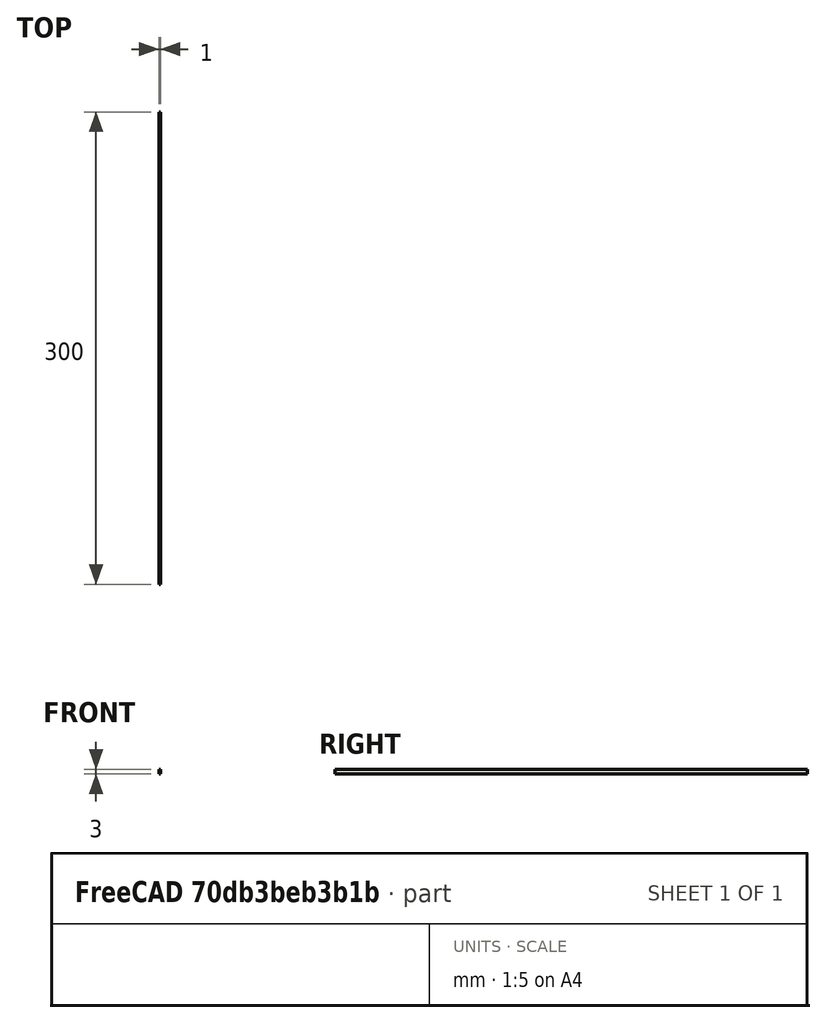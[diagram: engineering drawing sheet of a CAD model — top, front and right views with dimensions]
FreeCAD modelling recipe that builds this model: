
FCSTD DOCUMENT  (FreeCAD 0.18R16110 (Git))
Label: prutok_red
License: All rights reserved
LicenseURL: http://en.wikipedia.org/wiki/All_rights_reserved
objects: Sketcher::SketchObject×1, PartDesign::Pad×1, PartDesign::Body×1
note: 4 computed .brp shape members not serialized (recipe doc carries the construction recipe); baked Part::Feature solids carry a one-line shape summary decoded from their .brp

FEATURE [Sketcher::SketchObject] Sketch
  MapMode = 5
  Placement = pos=(0,0,0) rot=(1,0,0;1.5708rad)
  Support = -> [XZ_Plane]
  sketch-geometry (4):
    g0: LineSegment StartX=0 StartY=0 StartZ=0 EndX=1 EndY=0 EndZ=0
    g1: LineSegment StartX=1 StartY=0 StartZ=0 EndX=1 EndY=3 EndZ=0
    g2: LineSegment StartX=1 StartY=3 StartZ=0 EndX=0 EndY=3 EndZ=0
    g3: LineSegment StartX=0 StartY=3 StartZ=0 EndX=0 EndY=0 EndZ=0
  constraints (11):
    c: Coincident(g0,g1)
    c: Coincident(g1,g2)
    c: Coincident(g2,g3)
    c: Coincident(g3,g0)
    c: Horizontal(g0)
    c: Horizontal(g2)
    c: Vertical(g1)
    c: Vertical(g3)
    c: DistanceX(g2,g2) = 1
    c: DistanceY(g1,g1) = 3
    c: Coincident(g0,g-1)
FEATURE [PartDesign::Pad] Pad
  Length = 300
  Length2 = 100
  Placement = pos=(0,0,0) rot=(1,0,0;1.5708rad)
  Profile = -> Sketch
  Type = 0
FEATURE [PartDesign::Body] Body
  Group = -> [Sketch,Pad]
  Origin = -> Origin
  Tip = -> Pad
